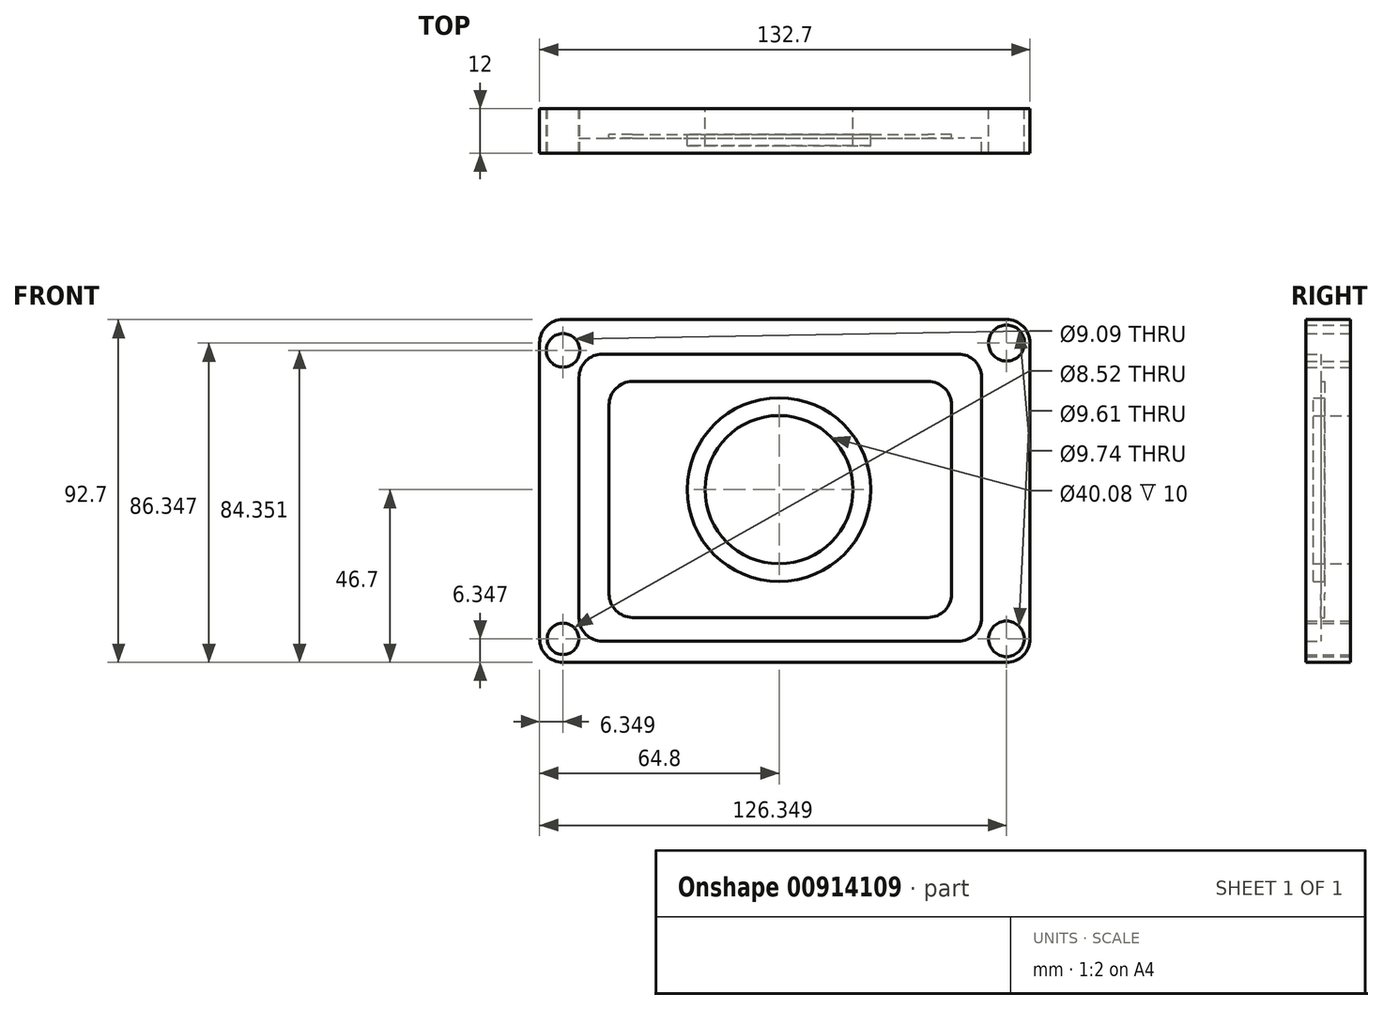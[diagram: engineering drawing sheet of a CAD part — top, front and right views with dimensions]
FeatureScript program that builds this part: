
annotation { "Feature Type Name" : "Feature", "Feature Type Description" : "" }
export const myFeature = defineFeature(function(context is Context, id is Id, definition is map)
    precondition{}
    {
        {
            var Q0;
            Q0=qCreatedBy(makeId("Front.planeOp"),FACE);
            var sketch = newSketch(context, id + "F0", { "sketchPlane" : qUnion([Q0])});
            skLineSegment(sketch, "E0.bottom", {"start": v(-58.45, 46) * mm, "end": v(61.55, 46) * mm});
            skLineSegment(sketch, "E0.top", {"start": v(-58.45, -46.7) * mm, "end": v(61.55, -46.7) * mm});
            skLineSegment(sketch, "E0.left", {"start": v(-64.8, 39.65) * mm, "end": v(-64.8, -40.35) * mm});
            skLineSegment(sketch, "E0.right", {"start": v(67.9, 39.65) * mm, "end": v(67.9, -40.35) * mm});
            skLineSegment(sketch, "E1.bottom", {"start": v(-47.76, 36.68) * mm, "end": v(48.5, 36.68) * mm});
            skLineSegment(sketch, "E1.top", {"start": v(-47.76, -41.02) * mm, "end": v(48.5, -41.02) * mm});
            skLineSegment(sketch, "E1.left", {"start": v(-54.1, 30.33) * mm, "end": v(-54.1, -34.67) * mm});
            skLineSegment(sketch, "E1.right", {"start": v(54.85, 30.33) * mm, "end": v(54.85, -34.67) * mm});
            skLineSegment(sketch, "E2.bottom", {"start": v(-39.65, 29.22) * mm, "end": v(40.35, 29.22) * mm});
            skLineSegment(sketch, "E2.top", {"start": v(-39.65, -34.57) * mm, "end": v(40.35, -34.57) * mm});
            skLineSegment(sketch, "E2.left", {"start": v(-46, 22.87) * mm, "end": v(-46, -28.22) * mm});
            skLineSegment(sketch, "E2.right", {"start": v(46.7, 22.87) * mm, "end": v(46.7, -28.22) * mm});
            skCircle(sketch, "E3", {"center": v(0, 0) * mm, "radius": 24.83 * mm});
            skCircle(sketch, "E4", {"center": v(0, 0) * mm, "radius": 20.04 * mm});
            skPoint(sketch, "E5.visualSharp", {"position": v(-64.8, 46) * mm});
            skArc(sketch, "E5.filletArc", {"start": v(-58.45, 46) * mm, "mid": v(-62.94, 44.14) * mm, "end": v(-64.8, 39.65) * mm});
            skPoint(sketch, "E6.visualSharp", {"position": v(-64.8, -46.7) * mm});
            skArc(sketch, "E6.filletArc", {"start": v(-64.8, -40.35) * mm, "mid": v(-62.94, -44.84) * mm, "end": v(-58.45, -46.7) * mm});
            skPoint(sketch, "E7.visualSharp", {"position": v(67.9, -46.7) * mm});
            skArc(sketch, "E7.filletArc", {"start": v(61.55, -46.7) * mm, "mid": v(66.04, -44.84) * mm, "end": v(67.9, -40.35) * mm});
            skPoint(sketch, "E8.visualSharp", {"position": v(67.9, 46) * mm});
            skArc(sketch, "E8.filletArc", {"start": v(67.9, 39.65) * mm, "mid": v(66.04, 44.14) * mm, "end": v(61.55, 46) * mm});
            skPoint(sketch, "E9.visualSharp", {"position": v(-54.1, 36.68) * mm});
            skArc(sketch, "E9.filletArc", {"start": v(-47.76, 36.68) * mm, "mid": v(-52.25, 34.82) * mm, "end": v(-54.1, 30.33) * mm});
            skPoint(sketch, "E10.visualSharp", {"position": v(-54.1, -41.02) * mm});
            skArc(sketch, "E10.filletArc", {"start": v(-54.1, -34.67) * mm, "mid": v(-52.25, -39.16) * mm, "end": v(-47.76, -41.02) * mm});
            skPoint(sketch, "E11.visualSharp", {"position": v(54.85, -41.02) * mm});
            skArc(sketch, "E11.filletArc", {"start": v(48.5, -41.02) * mm, "mid": v(52.99, -39.16) * mm, "end": v(54.85, -34.67) * mm});
            skPoint(sketch, "E12.visualSharp", {"position": v(54.85, 36.68) * mm});
            skArc(sketch, "E12.filletArc", {"start": v(54.85, 30.33) * mm, "mid": v(52.99, 34.82) * mm, "end": v(48.5, 36.68) * mm});
            skPoint(sketch, "E13.visualSharp", {"position": v(-46, -34.57) * mm});
            skArc(sketch, "E13.filletArc", {"start": v(-46, -28.22) * mm, "mid": v(-44.14, -32.7) * mm, "end": v(-39.65, -34.57) * mm});
            skPoint(sketch, "E14.visualSharp", {"position": v(-46, 29.22) * mm});
            skArc(sketch, "E14.filletArc", {"start": v(-39.65, 29.22) * mm, "mid": v(-44.14, 27.36) * mm, "end": v(-46, 22.87) * mm});
            skPoint(sketch, "E15.visualSharp", {"position": v(46.7, 29.22) * mm});
            skArc(sketch, "E15.filletArc", {"start": v(46.7, 22.87) * mm, "mid": v(44.84, 27.36) * mm, "end": v(40.35, 29.22) * mm});
            skPoint(sketch, "E16.visualSharp", {"position": v(46.7, -34.57) * mm});
            skArc(sketch, "E16.filletArc", {"start": v(40.35, -34.57) * mm, "mid": v(44.84, -32.7) * mm, "end": v(46.7, -28.22) * mm});
            skCircle(sketch, "E17", {"center": v(-58.45, 37.65) * mm, "radius": 4.54 * mm});
            skCircle(sketch, "E18", {"center": v(-58.45, -40.35) * mm, "radius": 4.26 * mm});
            skCircle(sketch, "E19", {"center": v(61.55, -40.35) * mm, "radius": 4.8 * mm});
            skCircle(sketch, "E20", {"center": v(61.55, 39.65) * mm, "radius": 4.87 * mm});
            skSolve(sketch);
        }
        {
            var Q0;
            Q0 = qSketchRegion(id + "F0", true);
            extrude(context, id + "F1", {"entities" : qUnion([Q0]), "depth" : 12 * mm, "offsetDistance" : 25 * mm});
        }
        {
            var Q0;
            Q0=makeQuery(id+"F0.imprint","IMPRINT",FACE,{"disambiguationData":[TD([[makeQuery(id+"F0.imprint","IMPRINT",EDGE,{"derivedFrom":sQuery(id+"F0.wireOp",EDGE,"E1.bottom")}),-1.0]])]});
            extrude(context, id + "F2", {"entities" : qUnion([Q0]), "operationType" : NewBodyOperationType.ADD, "depth" : 8 * mm, "offsetDistance" : 25 * mm});
        }
        {
            var Q0;
            Q0=makeQuery(id+"F0.imprint","IMPRINT",FACE,{"disambiguationData":[TD([[makeQuery(id+"F0.imprint","IMPRINT",EDGE,{"derivedFrom":sQuery(id+"F0.wireOp",EDGE,"E2.bottom")}),-1.0]])]});
            extrude(context, id + "F3", {"entities" : qUnion([Q0]), "operationType" : NewBodyOperationType.ADD, "depth" : 7 * mm, "offsetDistance" : 25 * mm});
        }
        {
            var Q0;
            Q0=makeQuery(id+"F0.imprint","IMPRINT",FACE,{"disambiguationData":[TD([[makeQuery(id+"F0.imprint","IMPRINT",EDGE,{"derivedFrom":sQuery(id+"F0.wireOp",EDGE,"E3")}),1.0]])]});
            extrude(context, id + "F4", {"entities" : qUnion([Q0]), "operationType" : NewBodyOperationType.ADD, "depth" : 10 * mm, "offsetDistance" : 25 * mm});
        }
    });
